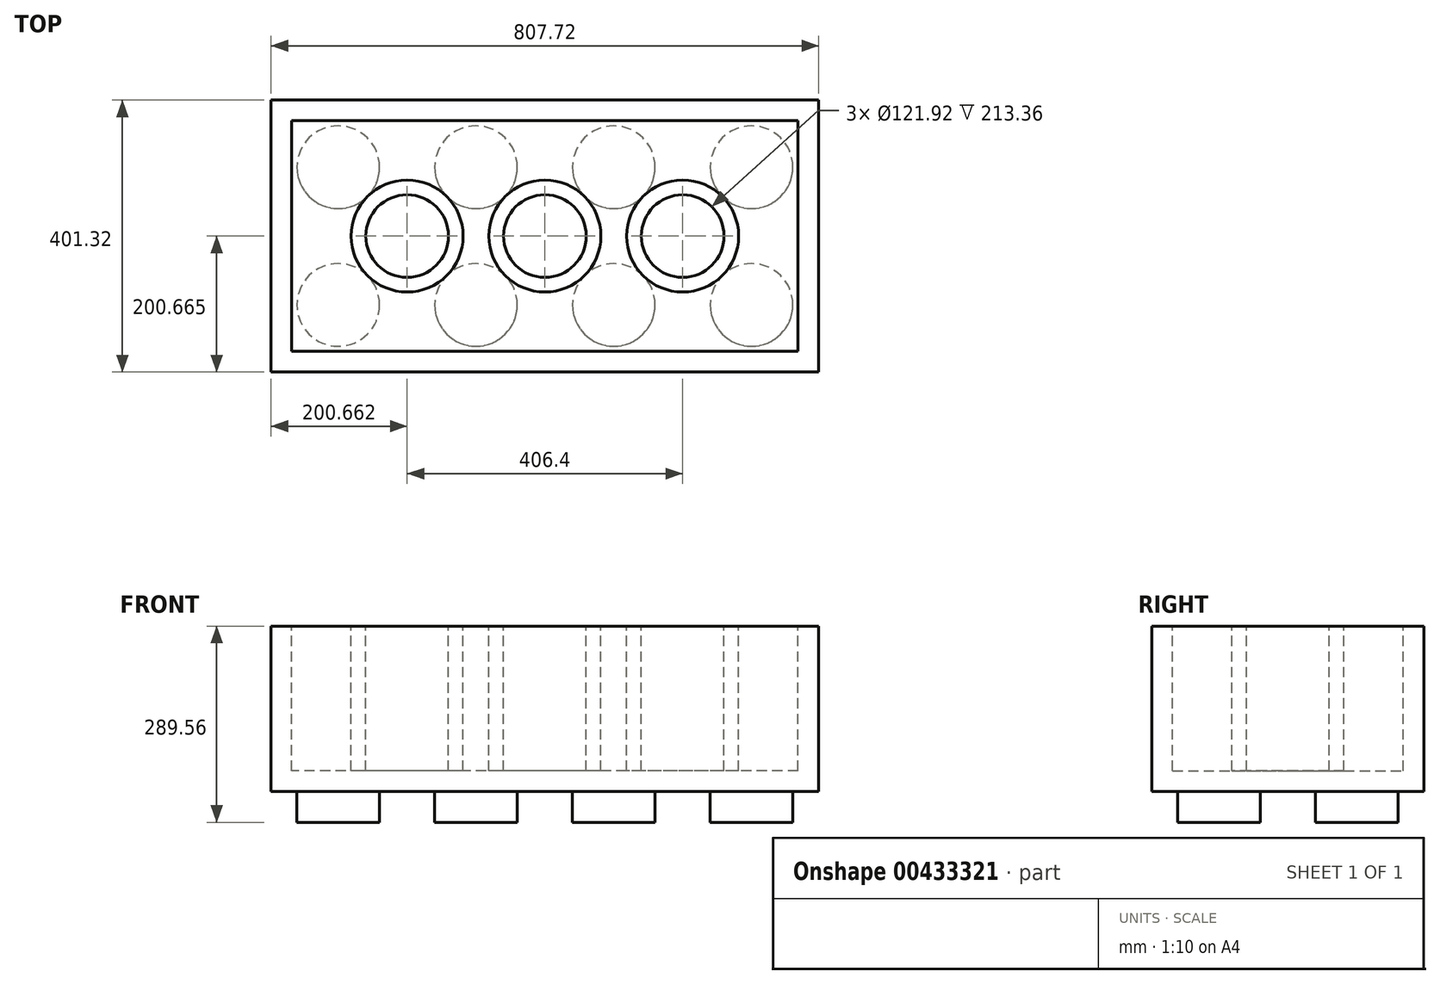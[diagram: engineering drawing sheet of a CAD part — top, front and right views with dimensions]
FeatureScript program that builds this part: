
annotation { "Feature Type Name" : "Feature", "Feature Type Description" : "" }
export const myFeature = defineFeature(function(context is Context, id is Id, definition is map)
    precondition{}
    {
        {
            var Q0;
            Q0=qCreatedBy(makeId("Top.planeOp"),FACE);
            var sketch = newSketch(context, id + "F0", { "sketchPlane" : qUnion([Q0])});
            skLineSegment(sketch, "E0.bottom", {"start": v(-378.63, 186) * mm, "end": v(429.1, 186) * mm});
            skLineSegment(sketch, "E0.top", {"start": v(-378.63, -215.32) * mm, "end": v(429.1, -215.32) * mm});
            skLineSegment(sketch, "E0.left", {"start": v(-378.63, 186) * mm, "end": v(-378.63, -215.32) * mm});
            skLineSegment(sketch, "E0.right", {"start": v(429.1, 186) * mm, "end": v(429.1, -215.32) * mm});
            skSolve(sketch);
        }
        {
            var Q0;
            Q0=makeQuery(id+"F0.imprint","IMPRINT",FACE,{"disambiguationData":[TD([[makeQuery(id+"F0.imprint","IMPRINT",EDGE,{"derivedFrom":sQuery(id+"F0.wireOp",EDGE,"E0.bottom")}),-1.0]])]});
            extrude(context, id + "F1", {"entities" : qUnion([Q0]), "oppositeDirection" : true, "depth" : 243.84 * mm});
        }
        {
            var Q0;
            Q0=makeQuery(id+"F1.opExtrude","CAP_FACE",FACE,{"disambiguationData":[OSD([sQuery(id+"F0.wireOp",EDGE,"E0.bottom"),sQuery(id+"F0.wireOp",EDGE,"E0.top"),sQuery(id+"F0.wireOp",EDGE,"E0.left"),sQuery(id+"F0.wireOp",EDGE,"E0.right")])],"isStart":false});
            var sketch = newSketch(context, id + "F2", { "sketchPlane" : qUnion([Q0])});
            skCircle(sketch, "E1", {"center": v(-279.57, 116.26) * mm, "radius": 60.96 * mm});
            skCircle(sketch, "E2.0.1.0", {"center": v(-279.57, -86.94) * mm, "radius": 60.96 * mm});
            skCircle(sketch, "E2.1.0.0", {"center": v(-76.37, 116.26) * mm, "radius": 60.96 * mm});
            skCircle(sketch, "E2.1.1.0", {"center": v(-76.37, -86.94) * mm, "radius": 60.96 * mm});
            skCircle(sketch, "E2.2.0.0", {"center": v(126.83, 116.26) * mm, "radius": 60.96 * mm});
            skCircle(sketch, "E2.2.1.0", {"center": v(126.83, -86.94) * mm, "radius": 60.96 * mm});
            skCircle(sketch, "E2.3.0.0", {"center": v(330.03, 116.26) * mm, "radius": 60.96 * mm});
            skCircle(sketch, "E2.3.1.0", {"center": v(330.03, -86.94) * mm, "radius": 60.96 * mm});
            skLineSegment(sketch, "E2.direction1", {"start": v(-279.57, 116.26) * mm, "end": v(-76.37, 116.26) * mm, "construction": true});
            skLineSegment(sketch, "E2.direction2", {"start": v(-279.57, 116.26) * mm, "end": v(-279.57, -86.94) * mm, "construction": true});
            skSolve(sketch);
        }
        {
            var Q0;
            Q0=qSketchRegion(id+"F2",true);
            extrude(context, id + "F3", {"entities" : qUnion([Q0]), "operationType" : NewBodyOperationType.ADD, "depth" : 45.72 * mm});
        }
        {
            var Q0;
            Q0=makeQuery(id+"F1.opExtrude","CAP_FACE",FACE,{"disambiguationData":[OSD([sQuery(id+"F0.wireOp",EDGE,"E0.bottom"),sQuery(id+"F0.wireOp",EDGE,"E0.top"),sQuery(id+"F0.wireOp",EDGE,"E0.left"),sQuery(id+"F0.wireOp",EDGE,"E0.right")])],"isStart":true});
            var sketch = newSketch(context, id + "F4", { "sketchPlane" : qUnion([Q0])});
            skCircle(sketch, "E3", {"center": v(-177.97, -14.66) * mm, "radius": 82.55 * mm});
            skCircle(sketch, "E4", {"center": v(-177.97, -14.66) * mm, "radius": 60.96 * mm});
            skCircle(sketch, "E5.1.0.0", {"center": v(25.23, -14.66) * mm, "radius": 60.96 * mm});
            skCircle(sketch, "E5.1.0.1", {"center": v(25.23, -14.66) * mm, "radius": 82.55 * mm});
            skCircle(sketch, "E5.2.0.0", {"center": v(228.43, -14.66) * mm, "radius": 60.96 * mm});
            skCircle(sketch, "E5.2.0.1", {"center": v(228.43, -14.66) * mm, "radius": 82.55 * mm});
            skLineSegment(sketch, "E5.direction1", {"start": v(-177.97, -14.66) * mm, "end": v(25.23, -14.66) * mm, "construction": true});
            skSolve(sketch);
        }
        {
            var Q0;
            Q0=makeQuery(id+"F4.imprint","IMPRINT",FACE,{"disambiguationData":[TD([[makeQuery(id+"F4.imprint","IMPRINT",EDGE,{"derivedFrom":sQuery(id+"F4.wireOp",EDGE,"E3")}),-1.0]])]});
            var sketch = newSketch(context, id + "F5", { "sketchPlane" : qUnion([Q0])});
            skLineSegment(sketch, "E6.bottom", {"start": v(-348.15, 155.52) * mm, "end": v(398.61, 155.52) * mm});
            skLineSegment(sketch, "E6.top", {"start": v(-348.15, -184.84) * mm, "end": v(398.61, -184.84) * mm});
            skLineSegment(sketch, "E6.left", {"start": v(-348.15, 155.52) * mm, "end": v(-348.15, -184.84) * mm});
            skLineSegment(sketch, "E6.right", {"start": v(398.61, 155.52) * mm, "end": v(398.61, -184.84) * mm});
            skSolve(sketch);
        }
        {
            var Q0;
            Q0=qSketchRegion(id+"F5",true);
            extrude(context, id + "F6", {"entities" : qUnion([Q0]), "operationType" : NewBodyOperationType.ADD, "oppositeDirection" : true, "depth" : 213.36 * mm});
        }
        {
            var Q0;
            Q0=makeQuery(id+"F4.imprint","IMPRINT",FACE,{"disambiguationData":[TD([[makeQuery(id+"F4.imprint","IMPRINT",EDGE,{"derivedFrom":sQuery(id+"F4.wireOp",EDGE,"E3")}),-1.0]])]});
            var sketch = newSketch(context, id + "F7", { "sketchPlane" : qUnion([Q0])});
            skLineSegment(sketch, "E7.bottom", {"start": v(398.61, -184.84) * mm, "end": v(-348.15, -184.84) * mm});
            skLineSegment(sketch, "E7.top", {"start": v(398.61, 155.52) * mm, "end": v(-348.15, 155.52) * mm});
            skLineSegment(sketch, "E7.left", {"start": v(398.61, -184.84) * mm, "end": v(398.61, 155.52) * mm});
            skLineSegment(sketch, "E7.right", {"start": v(-348.15, -184.84) * mm, "end": v(-348.15, 155.52) * mm});
            skSolve(sketch);
        }
        {
            var Q0;
            Q0=makeQuery(id+"F7.imprint","IMPRINT",FACE,{"disambiguationData":[TD([[makeQuery(id+"F7.imprint","IMPRINT",EDGE,{"derivedFrom":sQuery(id+"F7.wireOp",EDGE,"E7.bottom")}),-1.0]])]});
            var Q1;
            Q1=makeQuery(id+"F4.imprint","IMPRINT",FACE,{"disambiguationData":[TD([[makeQuery(id+"F4.imprint","IMPRINT",EDGE,{"derivedFrom":sQuery(id+"F4.wireOp",EDGE,"E5.2.0.0")}),1.0]])]});
            var Q2;
            Q2=makeQuery(id+"F4.imprint","IMPRINT",FACE,{"disambiguationData":[TD([[makeQuery(id+"F4.imprint","IMPRINT",EDGE,{"derivedFrom":sQuery(id+"F4.wireOp",EDGE,"E4")}),1.0]])]});
            var Q3;
            Q3=makeQuery(id+"F4.imprint","IMPRINT",FACE,{"disambiguationData":[TD([[makeQuery(id+"F4.imprint","IMPRINT",EDGE,{"derivedFrom":sQuery(id+"F4.wireOp",EDGE,"E5.1.0.0")}),1.0]])]});
            extrude(context, id + "F8", {"entities" : qUnion([Q0, Q1, Q2, Q3]), "operationType" : NewBodyOperationType.REMOVE, "oppositeDirection" : true, "depth" : 213.36 * mm});
        }
    });
